# Revit family: Gira_066166
name_source: partatom
category: Electrical Fixtures
revit_build: Autodesk Revit 2017 (Build: 20160225_1515(x64)
units: mm (PartAtom-declared; Revit-internal decimal feet)

## family parameters
Cut with Voids When Loaded = No
Host = Face
Maintain Annotation Orientation = Yes
Part Type = Normal
Room Calculation Point = No
Round Connector Dimension = Use Diameter
Shared = No

## types (1)
- Auto.ctrl.sw. Komfort 1.10 m Gira TX_44 (WP FM) p.white
    Available = No
    BIM (1) = https://media.stage.bim.site
    Category = Sensor element for movement sensor
    Data sheet (1) = https://katalog.gira.de
    Default Elevation = 1219 mm
    Description = ACS Kmf.1.10m TX_44 PW,System  2000 automatic control switch Komfort top unit mounting height up to 1.10 m,Komfort top unit,pure white,Features:,- In conjunction with a System 2000 switching insert, the automatic control switch can be set to short-term operation. Short-term operation is brightness-independent and can be used to control a bell, for example.,- When a System 2000 dimming insert is used, when the set delay time elapses, the lighting is continuously dimmed to the minimum brightness within 30 seconds and then switched off.,- A memory value can be saved using a System 2000 auxiliary unit which is switched on when motion is detected.,- The current ambient brightness is easily saved as a brightness switching threshold using a teach-in function.,- Switchable to permanent-on, permanent-off, or automatic mode using a slider switch.,,Notes :,- Suitable for indoor use only.,- At an mounting height of 1.10 m, the horizontal detection field has no natural limit if used outdoors. Use the System 2000 automatic control switch mounting height up to 2.20 for outdoor use.,- The System 2000 automatic control switch top units can be operated with the System 2000 inserts as of release R2.
    GTIN = 4010337661665
    HAN = 066166
    HeinzeBIM = https://bimportal.heinze.de
    Manufacturer = Gira
    Manufacturer URL = https://www.gira.de
    Model = Movement sensor
    Name = Auto.ctrl.sw. Komfort 1.10 m Gira TX_44 (WP FM) p.white
    URL = http://katalog.gira.de

## geometry (parser evidence)
native form markers: Blend x2, Sweep x2
no freeform markers — native parametric forms only
